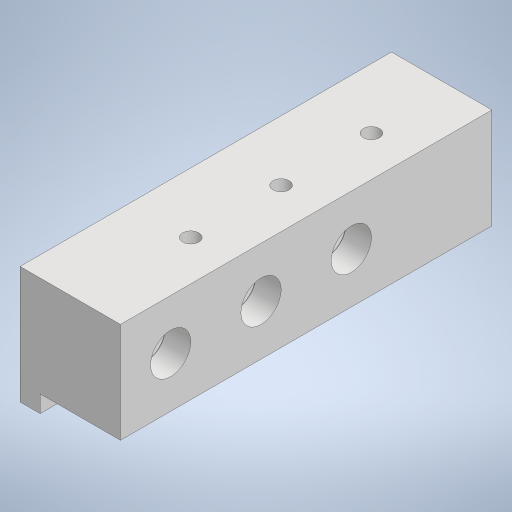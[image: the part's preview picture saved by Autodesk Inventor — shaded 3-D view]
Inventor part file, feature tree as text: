
AUTODESK INVENTOR PART (.ipt)
format: ipt  version: 2024.1 (Build 281209000, 209)  size: 283,648 bytes
history: native  units: in
note: dims shown in document units (in); Inventor stores cm internally (conversion verified against a paired STEP export)
features: extrude x7, sketch x7, chamfer x1
ambient origin geometry x8: Origin, YZ Plane, XZ Plane, XY Plane, X Axis, Y Axis, Z Axis, Center Point
bodies: Solid1 (feature_tree)
feature tree (15):
  extrude  "Extrusion1"  Depth=0.3937in
  extrude  "Extrusion2"  Depth=0.0787in
  extrude  "Extrusion3"  Depth=0.0669in
  extrude  "Extrusion4"  Depth=0.315in
  extrude  "Extrusion5"  Depth=0.1575in
  chamfer  "Chamfer1"  [1 undecoded]
  extrude  "Extrusion6"  Depth=0.315in
  extrude  "Extrusion7"  Depth=0.315in
  sketch  "Sketch1"  dims[d0=1.1024in d1=0.3937in]
  sketch  "Sketch2"  dims[d2=0.3937in d3=0.0in d4=0.0787in]
  sketch  "Sketch3"  dims[d5=0.0669in d6=0.0in d7=0.063in]
  sketch  "Sketch4"  dims[d8=0.063in d9=0.315in]
  sketch  "Sketch5"  dims[d10=0.3543in d11=0.1575in]
  sketch  "Sketch6"  dims[d12=0.1575in d13=0.0in d14=0.0in]
  sketch  "Sketch7"  dims[d15=0.0827in d16=0.0827in d17=0.0827in d18=0.1969in d19=0.1969in d20=0.1969in d21=0.1969in d22=0.3543in d23=0.3543in d24=0.0in d25=0.0in d26=0.1575in d27=0.1575in d28=0.1575in d29=0.0984in d30=0.0in d31=0.0354in d32=0.0787in d33=45.0deg d34=0.3543in d35=0.0in d39=0.063in d40=0.1575in d41=0.315in d42=0.0in d43=0.0in]
note: 1 required parameter value undecoded (feature->parameter linkage not recoverable at this tier; creation-order binding heuristic only, values carry confidence <= 0.55)
